# Revit family: BE_88065_de_DE
name_source: partatom
category: Leuchten
revit_build: Autodesk Revit 2015 (Build: 20150704_0715(x64)
units: mm (PartAtom-declared; Revit-internal decimal feet)

## types (4) — shared parameters
AC/DC = AC/DC
Aktualisierung = 2015-11-11T04:07:44
BEGA_Dummy = Nein
BEGA_IES = Ja
BEGA_Intern = Ja
BEGA_Intern_Konstruktion = Ja
BEGA_Intern_an = Ja
BEGA_Intern_aus = Ja
Beschreibung = Lichtbauelement
Beschreibung_Sonderanfertigung = Hier können Sie Informationen zur Sonderanfertigung eintragen.
CE_Konformität = ja
Energieeffizienzklasse = LED A++ - A
Farbfilter = 16777215
Farbtemperaturverschiebung bei Dämpfen der Lampe = <Keine Auswahl>
Farbwiedergabeindex = Ra > 80
Frequenz = 0/50-60 Hz
Gewicht = 57.9 kg
Hersteller = BEGA
Lampe = LED 47.7 W
Lastklassifizierung = Beleuchtung
Lebensdauerkriterien = L70 = 50.000 h
Leuchtenlichtstrom = 5776 lm
Logo = BEGA_Logo.png
Material_02 = BEGA_Oberfläche_Silber_matt
Material_06 = BEGA_Oberfläche_Edelstahl_gebürstet
Material_12 = BEGA_Kunststoff_klar
Material_15 = BEGA_Leuchtmedium_matt
Material_17 = BEGA_Reflektor
Material_19 = BEGA_Dummy_matt
Neigungswinkel = 0.00°
Produktdatenblatt = http://www.bega.de
Scheinlast = 0 VA
Schutzart = IP 65
Schutzklasse = I
Sonderanfertigung = Nein
Spannung = 0 V
Typenbild = 88065.png
URL = http://www.bega.de
Umgebungstemperatur = 25 °C
Windangriffsfläche = 1.1 m²
zero-valued in all types: Vorgabe-Ansicht

## per-type parameters (varying)
| type | Bestellnummer | Datei für fotometrisches Netz | Farbtemperatur | LED_Modulbezeichnung | Lampenlichtstrom | M_A | M_G | Modell |
| BEGA_88065_Silber_K4 | 88065A | BE_88065.IES | 4000 K | LED-0501/840 | 8190 lm | Ja | Nein | 88065A |
| BEGA_88065_Silber_K3 | 88065AK3 | BE_88065K3.IES | 3000 K | LED-0501/830 | 7810 lm | Ja | Nein | 88065AK3 |
| BEGA_88065_Grafit_K3 | 88065K3 | BE_88065K3.IES | 3000 K | LED-0501/830 | 7810 lm | Nein | Ja | 88065K3 |
| BEGA_88065_Grafit_K4 | 88065 | BE_88065.IES | 4000 K | LED-0501/840 | 8190 lm | Nein | Ja | 88065 |
